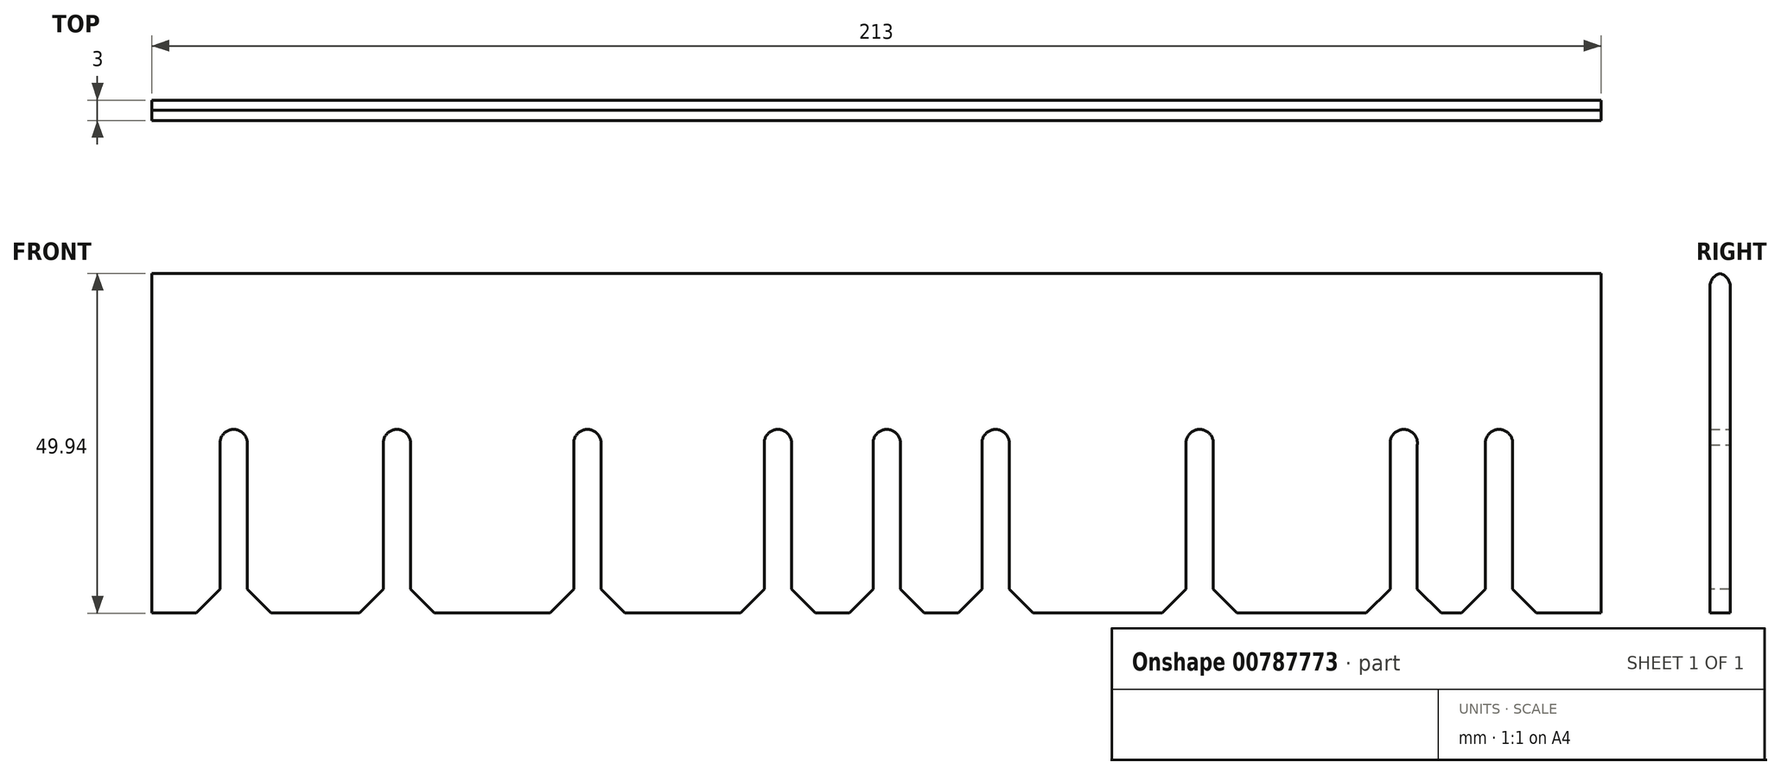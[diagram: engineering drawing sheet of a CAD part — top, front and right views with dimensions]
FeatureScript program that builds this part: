
annotation { "Feature Type Name" : "Feature", "Feature Type Description" : "" }
export const myFeature = defineFeature(function(context is Context, id is Id, definition is map)
    precondition{}
    {
        {
            var Q0;
            Q0=qCreatedBy(makeId("Front.planeOp"),FACE);
            var sketch = newSketch(context, id + "F0", { "sketchPlane" : qUnion([Q0])});
            skLineSegment(sketch, "E0.bottom", {"start": v(-82.52, 16.12) * mm, "end": v(130.48, 16.12) * mm});
            skLineSegment(sketch, "E0.left", {"start": v(-82.52, 16.12) * mm, "end": v(-82.52, -33.88) * mm});
            skLineSegment(sketch, "E0.right", {"start": v(130.48, 16.12) * mm, "end": v(130.48, -33.88) * mm});
            skLineSegment(sketch, "E1", {"start": v(-82.52, -33.88) * mm, "end": v(-72.52, -33.88) * mm});
            skLineSegment(sketch, "E2.left", {"start": v(-72.52, -33.88) * mm, "end": v(-72.52, -8.88) * mm});
            skLineSegment(sketch, "E2.right", {"start": v(-68.52, -33.88) * mm, "end": v(-68.52, -8.88) * mm});
            skArc(sketch, "E3", {"start": v(-72.52, -8.88) * mm, "mid": v(-70.38, -6.87) * mm, "end": v(-68.52, -9.14) * mm});
            skLineSegment(sketch, "E4.left", {"start": v(-48.52, -33.88) * mm, "end": v(-48.52, -8.88) * mm});
            skLineSegment(sketch, "E4.right", {"start": v(-44.52, -33.88) * mm, "end": v(-44.52, -8.88) * mm});
            skArc(sketch, "E5", {"start": v(-48.52, -8.88) * mm, "mid": v(-46.38, -6.87) * mm, "end": v(-44.52, -9.14) * mm});
            skLineSegment(sketch, "E6.left", {"start": v(-20.52, -33.88) * mm, "end": v(-20.52, -8.88) * mm});
            skLineSegment(sketch, "E6.right", {"start": v(-16.52, -33.88) * mm, "end": v(-16.52, -8.88) * mm});
            skArc(sketch, "E7", {"start": v(-20.52, -8.88) * mm, "mid": v(-18.38, -6.87) * mm, "end": v(-16.52, -9.14) * mm});
            skLineSegment(sketch, "E8.left", {"start": v(7.48, -33.88) * mm, "end": v(7.48, -8.88) * mm});
            skLineSegment(sketch, "E8.right", {"start": v(11.48, -33.88) * mm, "end": v(11.48, -8.88) * mm});
            skArc(sketch, "E9", {"start": v(7.48, -8.88) * mm, "mid": v(9.62, -6.87) * mm, "end": v(11.48, -9.14) * mm});
            skLineSegment(sketch, "E10.left", {"start": v(23.48, -33.88) * mm, "end": v(23.48, -8.88) * mm});
            skLineSegment(sketch, "E10.right", {"start": v(27.48, -33.88) * mm, "end": v(27.48, -8.88) * mm});
            skArc(sketch, "E11", {"start": v(23.48, -8.88) * mm, "mid": v(25.62, -6.87) * mm, "end": v(27.48, -9.14) * mm});
            skLineSegment(sketch, "E12.left", {"start": v(39.48, -33.88) * mm, "end": v(39.48, -8.88) * mm});
            skLineSegment(sketch, "E12.right", {"start": v(43.48, -33.88) * mm, "end": v(43.48, -8.88) * mm});
            skArc(sketch, "E13", {"start": v(39.48, -8.88) * mm, "mid": v(41.62, -6.87) * mm, "end": v(43.48, -9.14) * mm});
            skLineSegment(sketch, "E14.left", {"start": v(69.48, -33.88) * mm, "end": v(69.48, -8.88) * mm});
            skLineSegment(sketch, "E14.right", {"start": v(73.48, -33.88) * mm, "end": v(73.48, -8.88) * mm});
            skArc(sketch, "E15", {"start": v(69.48, -8.88) * mm, "mid": v(71.62, -6.87) * mm, "end": v(73.48, -9.14) * mm});
            skLineSegment(sketch, "E16.left", {"start": v(99.48, -33.88) * mm, "end": v(99.48, -8.88) * mm});
            skLineSegment(sketch, "E16.right", {"start": v(103.48, -33.88) * mm, "end": v(103.48, -8.88) * mm});
            skArc(sketch, "E17", {"start": v(99.48, -8.88) * mm, "mid": v(101.62, -6.87) * mm, "end": v(103.48, -9.14) * mm});
            skLineSegment(sketch, "E18.left", {"start": v(113.48, -33.88) * mm, "end": v(113.48, -8.88) * mm});
            skLineSegment(sketch, "E18.right", {"start": v(117.48, -33.88) * mm, "end": v(117.48, -8.88) * mm});
            skArc(sketch, "E19", {"start": v(113.48, -8.88) * mm, "mid": v(115.62, -6.87) * mm, "end": v(117.48, -9.14) * mm});
            skLineSegment(sketch, "E20.trimOffspring", {"start": v(-68.52, -33.88) * mm, "end": v(-48.52, -33.88) * mm});
            skLineSegment(sketch, "E21.trimOffspring", {"start": v(-44.52, -33.88) * mm, "end": v(-20.52, -33.88) * mm});
            skLineSegment(sketch, "E22.trimOffspring", {"start": v(-16.52, -33.88) * mm, "end": v(7.48, -33.88) * mm});
            skLineSegment(sketch, "E23.trimOffspring", {"start": v(11.48, -33.88) * mm, "end": v(23.48, -33.88) * mm});
            skLineSegment(sketch, "E24.trimOffspring", {"start": v(27.48, -33.88) * mm, "end": v(39.48, -33.88) * mm});
            skLineSegment(sketch, "E25.trimOffspring", {"start": v(43.48, -33.88) * mm, "end": v(69.48, -33.88) * mm});
            skLineSegment(sketch, "E26.trimOffspring", {"start": v(73.48, -33.88) * mm, "end": v(99.48, -33.88) * mm});
            skLineSegment(sketch, "E27.trimOffspring", {"start": v(103.48, -33.88) * mm, "end": v(113.48, -33.88) * mm});
            skLineSegment(sketch, "E28.trimOffspring", {"start": v(117.48, -33.88) * mm, "end": v(130.48, -33.88) * mm});
            skSolve(sketch);
        }
        {
            var Q0;
            Q0 = qSketchRegion(id + "F0", true);
            extrude(context, id + "F1", {"entities" : qUnion([Q0]), "depth" : 3 * mm, "offsetDistance" : 25 * mm});
        }
        {
            var Q0;
            Q0=makeQuery(id+"F1.opExtrude","SWEPT_EDGE",EDGE,{"disambiguationData":[OSD([sQuery(id+"F0.wireOp",EDGE,"E1"),sQuery(id+"F0.wireOp",EDGE,"E2.left")])]});
            var Q1;
            Q1=makeQuery(id+"F1.opExtrude","SWEPT_EDGE",EDGE,{"disambiguationData":[OSD([sQuery(id+"F0.wireOp",EDGE,"E4.left"),sQuery(id+"F0.wireOp",EDGE,"E20.trimOffspring")])]});
            var Q2;
            Q2=makeQuery(id+"F1.opExtrude","SWEPT_EDGE",EDGE,{"disambiguationData":[OSD([sQuery(id+"F0.wireOp",EDGE,"E6.left"),sQuery(id+"F0.wireOp",EDGE,"E21.trimOffspring")])]});
            var Q3;
            Q3=makeQuery(id+"F1.opExtrude","SWEPT_EDGE",EDGE,{"disambiguationData":[OSD([sQuery(id+"F0.wireOp",EDGE,"E8.left"),sQuery(id+"F0.wireOp",EDGE,"E22.trimOffspring")])]});
            var Q4;
            Q4=makeQuery(id+"F1.opExtrude","SWEPT_EDGE",EDGE,{"disambiguationData":[OSD([sQuery(id+"F0.wireOp",EDGE,"E10.left"),sQuery(id+"F0.wireOp",EDGE,"E23.trimOffspring")])]});
            var Q5;
            Q5=makeQuery(id+"F1.opExtrude","SWEPT_EDGE",EDGE,{"disambiguationData":[OSD([sQuery(id+"F0.wireOp",EDGE,"E12.left"),sQuery(id+"F0.wireOp",EDGE,"E24.trimOffspring")])]});
            var Q6;
            Q6=makeQuery(id+"F1.opExtrude","SWEPT_EDGE",EDGE,{"disambiguationData":[OSD([sQuery(id+"F0.wireOp",EDGE,"E14.left"),sQuery(id+"F0.wireOp",EDGE,"E25.trimOffspring")])]});
            var Q7;
            Q7=makeQuery(id+"F1.opExtrude","SWEPT_EDGE",EDGE,{"disambiguationData":[OSD([sQuery(id+"F0.wireOp",EDGE,"E16.left"),sQuery(id+"F0.wireOp",EDGE,"E26.trimOffspring")])]});
            var Q8;
            Q8=makeQuery(id+"F1.opExtrude","SWEPT_EDGE",EDGE,{"disambiguationData":[OSD([sQuery(id+"F0.wireOp",EDGE,"E18.left"),sQuery(id+"F0.wireOp",EDGE,"E27.trimOffspring")])]});
            var Q9;
            Q9=makeQuery(id+"F1.opExtrude","SWEPT_EDGE",EDGE,{"disambiguationData":[OSD([sQuery(id+"F0.wireOp",EDGE,"E16.right"),sQuery(id+"F0.wireOp",EDGE,"E27.trimOffspring")])]});
            var Q10;
            Q10=makeQuery(id+"F1.opExtrude","SWEPT_EDGE",EDGE,{"disambiguationData":[OSD([sQuery(id+"F0.wireOp",EDGE,"E18.right"),sQuery(id+"F0.wireOp",EDGE,"E28.trimOffspring")])]});
            var Q11;
            Q11=makeQuery(id+"F1.opExtrude","SWEPT_EDGE",EDGE,{"disambiguationData":[OSD([sQuery(id+"F0.wireOp",EDGE,"E14.right"),sQuery(id+"F0.wireOp",EDGE,"E26.trimOffspring")])]});
            var Q12;
            Q12=makeQuery(id+"F1.opExtrude","SWEPT_EDGE",EDGE,{"disambiguationData":[OSD([sQuery(id+"F0.wireOp",EDGE,"E12.right"),sQuery(id+"F0.wireOp",EDGE,"E25.trimOffspring")])]});
            var Q13;
            Q13=makeQuery(id+"F1.opExtrude","SWEPT_EDGE",EDGE,{"disambiguationData":[OSD([sQuery(id+"F0.wireOp",EDGE,"E10.right"),sQuery(id+"F0.wireOp",EDGE,"E24.trimOffspring")])]});
            var Q14;
            Q14=makeQuery(id+"F1.opExtrude","SWEPT_EDGE",EDGE,{"disambiguationData":[OSD([sQuery(id+"F0.wireOp",EDGE,"E8.right"),sQuery(id+"F0.wireOp",EDGE,"E23.trimOffspring")])]});
            var Q15;
            Q15=makeQuery(id+"F1.opExtrude","SWEPT_EDGE",EDGE,{"disambiguationData":[OSD([sQuery(id+"F0.wireOp",EDGE,"E6.right"),sQuery(id+"F0.wireOp",EDGE,"E22.trimOffspring")])]});
            var Q16;
            Q16=makeQuery(id+"F1.opExtrude","SWEPT_EDGE",EDGE,{"disambiguationData":[OSD([sQuery(id+"F0.wireOp",EDGE,"E4.right"),sQuery(id+"F0.wireOp",EDGE,"E21.trimOffspring")])]});
            var Q17;
            Q17=makeQuery(id+"F1.opExtrude","SWEPT_EDGE",EDGE,{"disambiguationData":[OSD([sQuery(id+"F0.wireOp",EDGE,"E2.right"),sQuery(id+"F0.wireOp",EDGE,"E20.trimOffspring")])]});
            chamfer(context, id + "F2", {"entities" : qUnion([Q0, Q1, Q2, Q3, Q4, Q5, Q6, Q7, Q8, Q9, Q10, Q11, Q12, Q13, Q14, Q15, Q16, Q17]), "width" : 3.5 * mm, "tangentPropagation" : true});
        }
        {
            var Q0;
            Q0=makeQuery(id+"F1.opExtrude","CAP_EDGE",EDGE,{"disambiguationData":[OSD([sQuery(id+"F0.wireOp",EDGE,"E0.bottom")])],"isStart":false});
            var Q1;
            Q1=makeQuery(id+"F1.opExtrude","CAP_EDGE",EDGE,{"disambiguationData":[OSD([sQuery(id+"F0.wireOp",EDGE,"E0.bottom")])],"isStart":true});
            fillet(context, id + "F3", {"entities" : qUnion([Q0, Q1]), "radius" : 2 * mm, "tangentPropagation" : true, "allowEdgeOverflow" : false});
        }
    });
